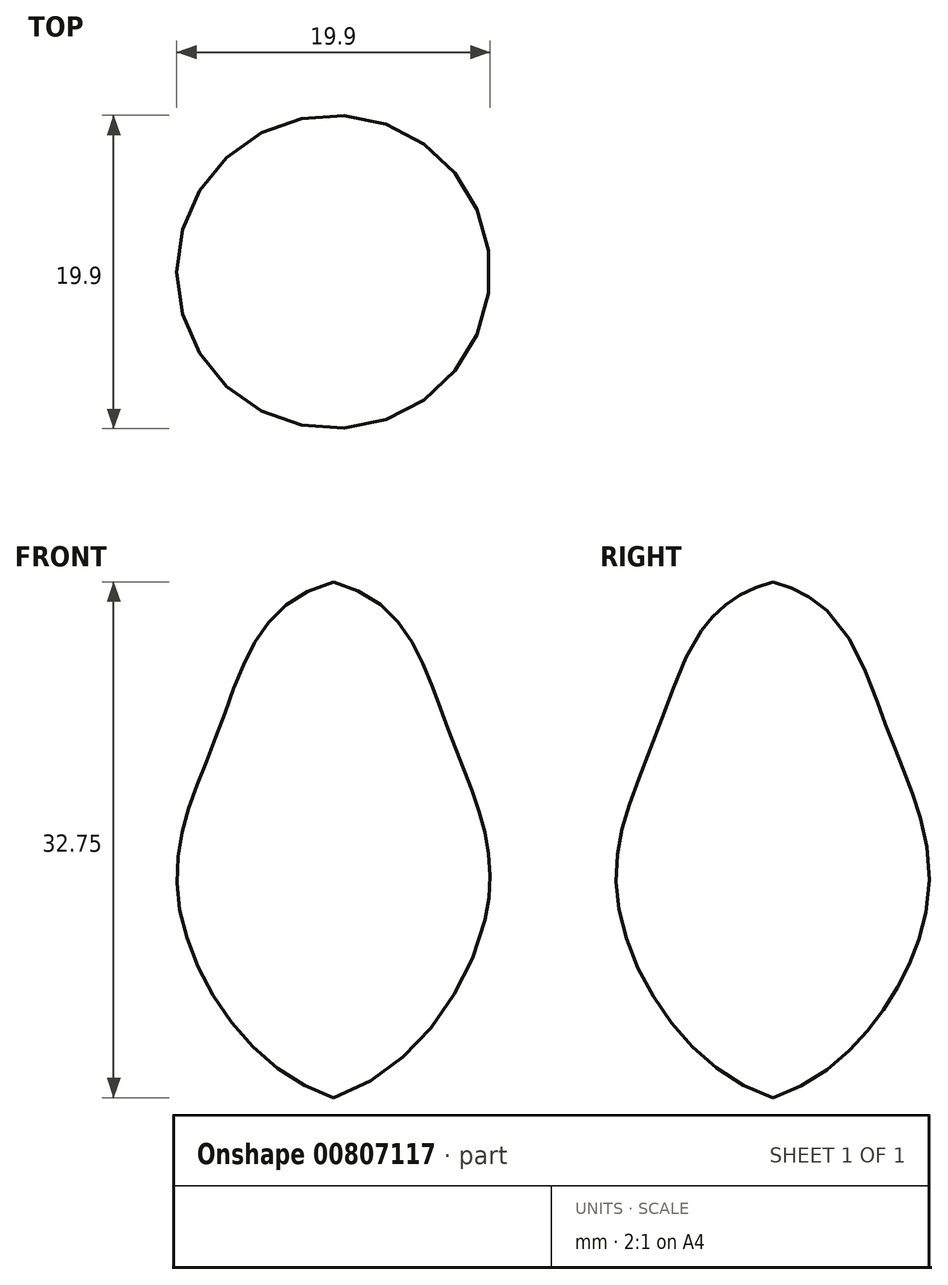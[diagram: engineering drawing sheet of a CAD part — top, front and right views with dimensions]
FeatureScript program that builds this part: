
annotation { "Feature Type Name" : "Feature", "Feature Type Description" : "" }
export const myFeature = defineFeature(function(context is Context, id is Id, definition is map)
    precondition{}
    {
        {
            var Q0;
            Q0=qCreatedBy(makeId("Front.planeOp"),FACE);
            var sketch = newSketch(context, id + "F0", { "sketchPlane" : qUnion([Q0])});
            skFitSpline(sketch, "E0", {"points": [v(0, 0) * mm, v(9.52, 2.16) * mm, v(2.83, 11.76) * mm, v(4.59, 25.84) * mm, v(11.85, 33.24) * mm, v(18.7, 48.4) * mm, v(16.26, 59.73) * mm, v(14.45, 38.18) * mm, v(-1.65, 32.16) * mm, v(-7.34, 23.24) * mm, v(-9.85, 12.47) * mm, v(0, 0) * mm]});
            skLineSegment(sketch, "E1", {"start": v(0, 75.37) * mm, "end": v(0, 0) * mm});
            skSolve(sketch);
        }
        {
            var Q0;
            {var subQ0=sQuery(id+"F0.wireOp",EDGE,"E1");var subQ1=sQuery(id+"F0.wireOp",EDGE,"E0");var subQ2=makeQuery(id+"F0.imprint","INTERSECT",VERTEX,{"disambiguationData":[OD(0.0)],"derivedFrom":[subQ1,subQ0]});Q0=makeQuery(id+"F0.imprint","IMPRINT",FACE,{"disambiguationData":[TD([[makeQuery(id+"F0.imprint","IMPRINT",EDGE,{"disambiguationData":[TD([[subQ2,-1.0]])],"derivedFrom":subQ1}),1.0]])]});}
            var Q1;
            Q1=sQuery(id+"F0.wireOp",EDGE,"E1");
            revolve(context, id + "F1", {"surfaceOperationType" : NewSurfaceOperationType.NEW, "entities" : qUnion([Q0]), "axis" : qUnion([Q1]), "revolveType" : RevolveType.FULL});
        }
    });
